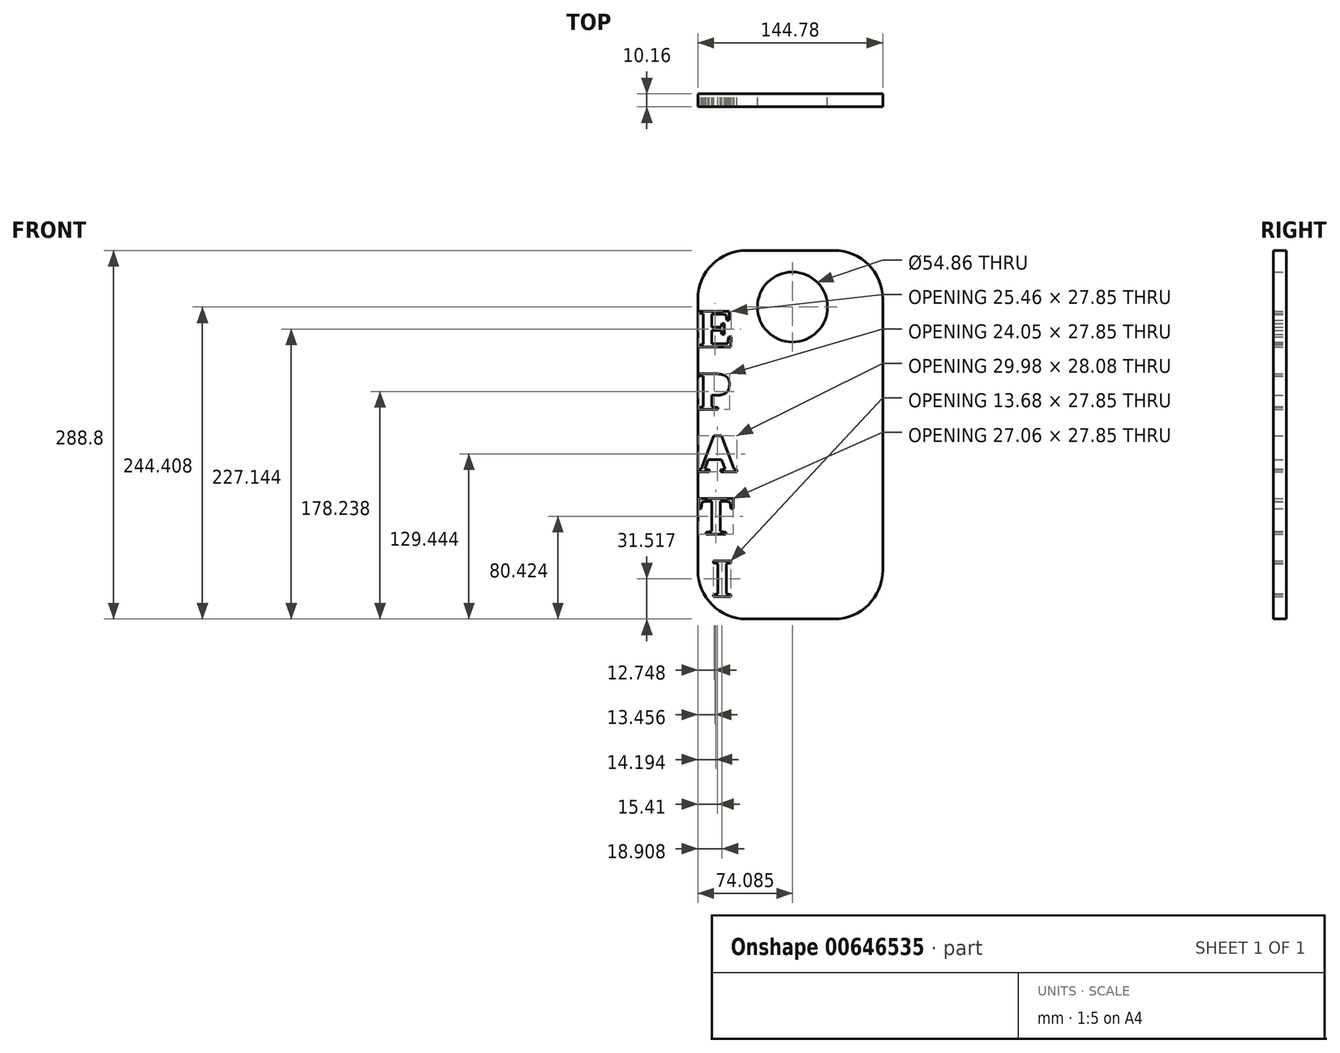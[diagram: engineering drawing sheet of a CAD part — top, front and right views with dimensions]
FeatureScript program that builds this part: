
annotation { "Feature Type Name" : "Feature", "Feature Type Description" : "" }
export const myFeature = defineFeature(function(context is Context, id is Id, definition is map)
    precondition{}
    {
        {
            var Q0;
            Q0=qCreatedBy(makeId("Front.planeOp"),FACE);
            var sketch = newSketch(context, id + "F0", { "sketchPlane" : qUnion([Q0])});
            skLineSegment(sketch, "E0.bottom", {"start": v(38.1, -76.58) * mm, "end": v(106.68, -76.58) * mm});
            skLineSegment(sketch, "E0.top", {"start": v(38.1, 212.22) * mm, "end": v(106.68, 212.22) * mm});
            skLineSegment(sketch, "E0.left", {"start": v(0, -38.48) * mm, "end": v(0, 174.12) * mm});
            skLineSegment(sketch, "E0.right", {"start": v(144.78, -38.48) * mm, "end": v(144.78, 174.12) * mm});
            skPoint(sketch, "E1.visualSharp", {"position": v(0, 212.22) * mm});
            skArc(sketch, "E1.filletArc", {"start": v(38.1, 212.22) * mm, "mid": v(11.16, 201.06) * mm, "end": v(0, 174.12) * mm});
            skPoint(sketch, "E2.visualSharp", {"position": v(144.78, 212.22) * mm});
            skArc(sketch, "E2.filletArc", {"start": v(144.78, 174.12) * mm, "mid": v(133.62, 201.06) * mm, "end": v(106.68, 212.22) * mm});
            skPoint(sketch, "E3.visualSharp", {"position": v(0, -76.58) * mm});
            skArc(sketch, "E3.filletArc", {"start": v(0, -38.48) * mm, "mid": v(11.16, -65.42) * mm, "end": v(38.1, -76.58) * mm});
            skPoint(sketch, "E4.visualSharp", {"position": v(144.78, -76.58) * mm});
            skArc(sketch, "E4.filletArc", {"start": v(106.68, -76.58) * mm, "mid": v(133.62, -65.42) * mm, "end": v(144.78, -38.48) * mm});
            skCircle(sketch, "E5", {"center": v(74.08, 167.83) * mm, "radius": 27.43 * mm});
            skText(sketch, "E6", { "text": "E\nP\nA\nT\n I", "fontName": "Tinos-Bold.ttf"});
            const initialGuessF0  = {"E6": [0, 0.13664, 1, 0, 0.03062]};
            skSetInitialGuess(sketch, initialGuessF0);
            skSolve(sketch);
        }
        {
            var Q0;
            Q0 = qSketchRegion(id + "F0", true);
            extrude(context, id + "F1", {"entities" : qUnion([Q0]), "depth" : 10.16 * mm, "offsetDistance" : 25.4 * mm});
        }
    });
